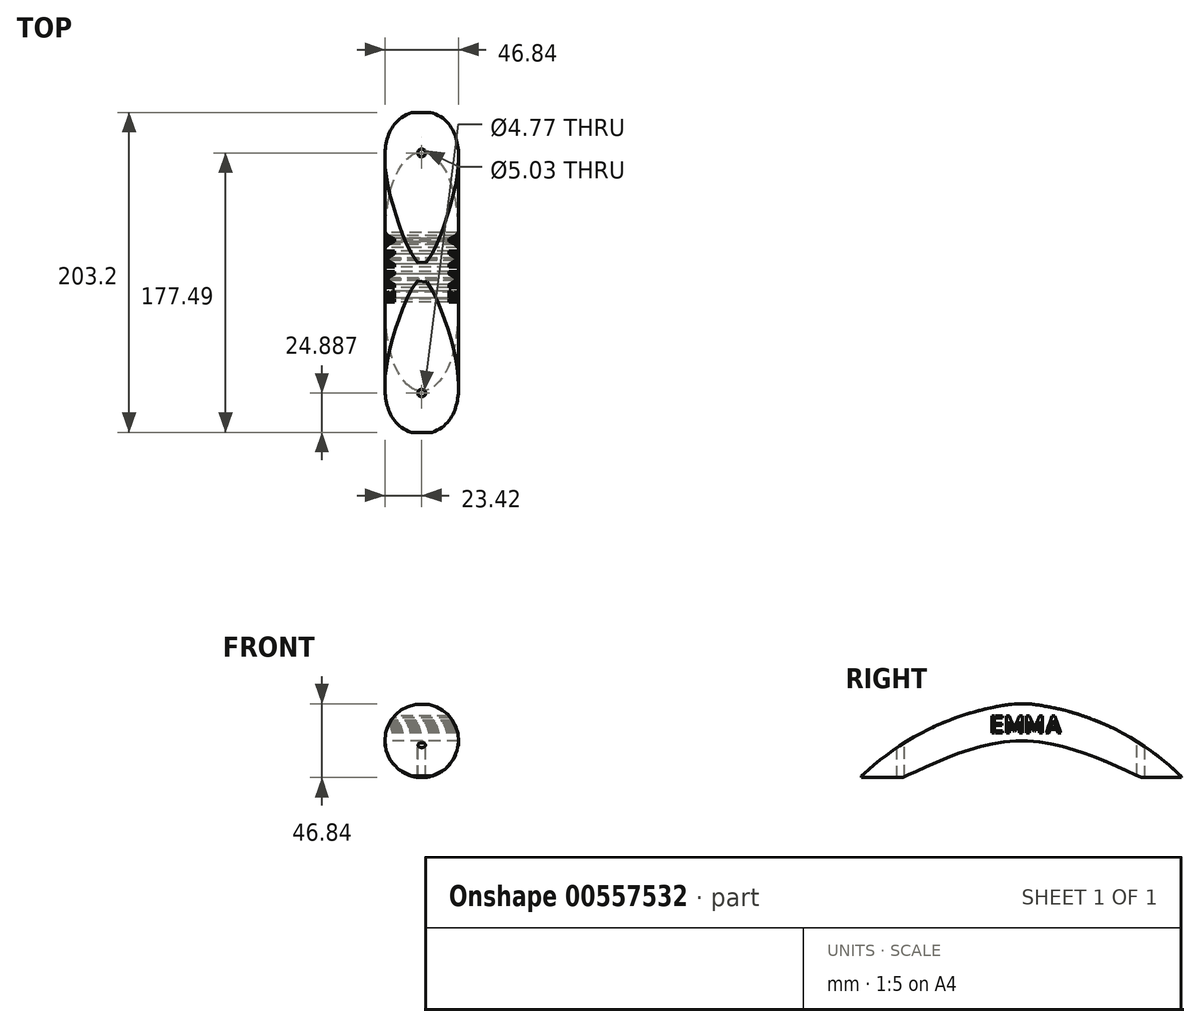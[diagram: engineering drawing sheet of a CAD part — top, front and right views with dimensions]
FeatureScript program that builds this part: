
annotation { "Feature Type Name" : "Feature", "Feature Type Description" : "" }
export const myFeature = defineFeature(function(context is Context, id is Id, definition is map)
    precondition{}
    {
        {
            var Q0;
            Q0=qCreatedBy(makeId("Front.planeOp"),FACE);
            var sketch = newSketch(context, id + "F0", { "sketchPlane" : qUnion([Q0])});
            skCircle(sketch, "E0", {"center": v(0, 0) * mm, "radius": 23.42 * mm});
            skSolve(sketch);
        }
        {
            var Q0;
            Q0 = qSketchRegion(id + "F0", true);
            extrude(context, id + "F1", {"entities" : qUnion([Q0]), "depth" : 101.6 * mm, "offsetDistance" : 25.4 * mm, "hasSecondDirection" : true, "secondDirectionOppositeDirection" : true, "secondDirectionDepth" : 101.6 * mm});
        }
        {
            var Q0;
            Q0=qCreatedBy(makeId("Right.planeOp"),FACE);
            var sketch = newSketch(context, id + "F2", { "sketchPlane" : qUnion([Q0])});
            skArc(sketch, "E1", {"start": v(0, 23.9) * mm, "mid": v(-54.84, 9.18) * mm, "end": v(-101.83, -22.71) * mm});
            skArc(sketch, "E2", {"start": v(102.42, -23.6) * mm, "mid": v(55.44, 9.27) * mm, "end": v(0, 23.9) * mm});
            skLineSegment(sketch, "E3", {"start": v(-101.83, -22.71) * mm, "end": v(-114, 31.91) * mm});
            skLineSegment(sketch, "E4", {"start": v(-114, 31.91) * mm, "end": v(108.96, 31.91) * mm});
            skLineSegment(sketch, "E5", {"start": v(108.96, 31.91) * mm, "end": v(102.42, -23.6) * mm});
            skFitSpline(sketch, "E6", {"points": [v(76.15, -23.3) * mm, v(0, 0) * mm, v(-76.45, -23.9) * mm], "startDerivative": vector(-152.48, 70.25) * mm, "endDerivative": vector(-152.71, -71.37) * mm});
            skLineSegment(sketch, "E7", {"start": v(76.15, -23.3) * mm, "end": v(0, -35.18) * mm});
            skLineSegment(sketch, "E8", {"start": v(0, -35.18) * mm, "end": v(-76.45, -23.9) * mm});
            skText(sketch, "E9", { "text": "EMMA", "fontName": "AllertaStencil-Regular.ttf"});
            const initialGuessF2  = {"E9": [-0.0202, 0.00484, 1, 0, 0.01094]};
            skSetInitialGuess(sketch, initialGuessF2);
            skSolve(sketch);
        }
        {
            var Q0;
            Q0 = qSketchRegion(id + "F2", true);
            extrude(context, id + "F3", {"entities" : qUnion([Q0]), "operationType" : NewBodyOperationType.REMOVE, "endBound" : BoundingType.SYMMETRIC, "depth" : 76.2 * mm, "offsetDistance" : 25.4 * mm});
        }
        {
            var Q0;
            Q0=qCreatedBy(makeId("Top.planeOp"),FACE);
            var sketch = newSketch(context, id + "F4", { "sketchPlane" : qUnion([Q0])});
            skCircle(sketch, "E10", {"center": v(0, -76.71) * mm, "radius": 5.85 * mm});
            skCircle(sketch, "E11", {"center": v(0, 75.89) * mm, "radius": 6.03 * mm});
            skCircle(sketch, "E12", {"center": v(0, -76.71) * mm, "radius": 2.38 * mm});
            skCircle(sketch, "E13", {"center": v(0, 75.89) * mm, "radius": 2.52 * mm});
            skSolve(sketch);
        }
        {
            var Q0;
            Q0=makeQuery(id+"F4.imprint","IMPRINT",FACE,{"disambiguationData":[TD([[makeQuery(id+"F4.imprint","IMPRINT",EDGE,{"derivedFrom":sQuery(id+"F4.wireOp",EDGE,"E13")}),1.0]])]});
            var Q1;
            Q1=makeQuery(id+"F4.imprint","IMPRINT",FACE,{"disambiguationData":[TD([[makeQuery(id+"F4.imprint","IMPRINT",EDGE,{"derivedFrom":sQuery(id+"F4.wireOp",EDGE,"E12")}),1.0]])]});
            extrude(context, id + "F5", {"entities" : qUnion([Q0, Q1]), "operationType" : NewBodyOperationType.REMOVE, "endBound" : BoundingType.THROUGH_ALL, "oppositeDirection" : true, "depth" : 25.4 * mm, "offsetDistance" : 25.4 * mm});
        }
        {
            var Q0;
            Q0=sQuery(id+"F4.wireOp",EDGE,"E11");
            var Q1;
            Q1=sQuery(id+"F4.wireOp",EDGE,"E10");
            extrude(context, id + "F6", {"bodyType" : ToolBodyType.SURFACE, "surfaceEntities" : qUnion([Q0, Q1]), "oppositeDirection" : true, "depth" : 7.62 * mm, "offsetDistance" : 25.4 * mm});
        }
    });
